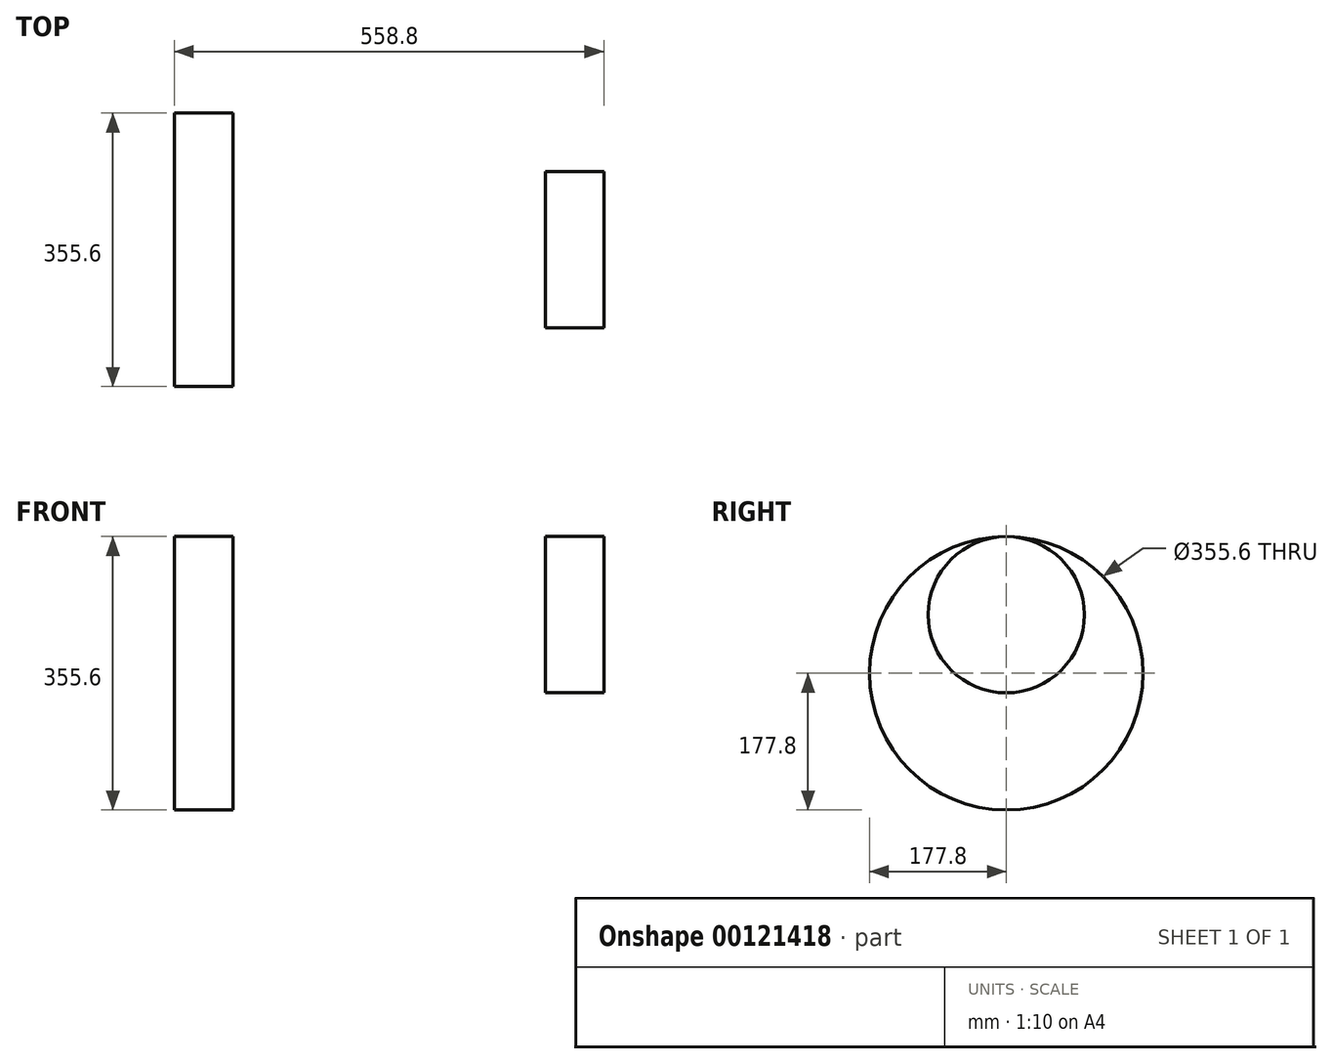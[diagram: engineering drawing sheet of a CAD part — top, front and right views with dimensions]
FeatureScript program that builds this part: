
annotation { "Feature Type Name" : "Feature", "Feature Type Description" : "" }
export const myFeature = defineFeature(function(context is Context, id is Id, definition is map)
    precondition{}
    {
        {
            var Q0;
            Q0=qCreatedBy(makeId("Right.planeOp"),FACE);
            cPlane(context, id + "F0", {"entities" : qUnion([Q0]), "cplaneType" : CPlaneType.OFFSET, "offset" : 406.4 * mm, "width" : 152.4 * mm, "height" : 152.4 * mm});
        }
        {
            var Q0;
            Q0=qCreatedBy(makeId("Front.planeOp"),FACE);
            var sketch = newSketch(context, id + "F1", { "sketchPlane" : qUnion([Q0])});
            skLineSegment(sketch, "E0.bottom", {"start": v(0, 203.2) * mm, "end": v(406.4, 203.2) * mm});
            skLineSegment(sketch, "E0.top", {"start": v(0, 0) * mm, "end": v(406.4, 0) * mm});
            skLineSegment(sketch, "E0.left", {"start": v(0, 203.2) * mm, "end": v(0, 0) * mm});
            skLineSegment(sketch, "E0.right", {"start": v(406.4, 203.2) * mm, "end": v(406.4, 0) * mm});
            skLineSegment(sketch, "E1.left", {"start": v(0, 0) * mm, "end": v(0, -152.4) * mm});
            skLineSegment(sketch, "E1.right", {"start": v(406.4, 0) * mm, "end": v(406.4, -152.4) * mm});
            skPoint(sketch, "E2", {"position": v(0, 0) * mm});
            skFitSpline(sketch, "E3", {"points": [v(0, -152.4) * mm, v(406.4, 0) * mm], "startDerivative": vector(696.83, 0) * mm, "endDerivative": vector(541.42, 0) * mm});
            skSolve(sketch);
        }
        {
            var Q0;
            Q0=qCreatedBy(makeId("Right.planeOp"),FACE);
            var sketch = newSketch(context, id + "F2", { "sketchPlane" : qUnion([Q0])});
            skCircle(sketch, "E4", {"center": v(0, 25.4) * mm, "radius": 177.8 * mm});
            skSolve(sketch);
        }
        {
            var Q0;
            Q0=qCreatedBy(id+"F0.planeOp",FACE);
            var sketch = newSketch(context, id + "F3", { "sketchPlane" : qUnion([Q0])});
            skCircle(sketch, "E5", {"center": v(0, 101.6) * mm, "radius": 101.6 * mm});
            skSolve(sketch);
        }
        {
            var Q0;
            Q0=sQuery(id+"F2.wireOp",EDGE,"E4");
            extrude(context, id + "F4", {"bodyType" : ToolBodyType.SURFACE, "surfaceEntities" : qUnion([Q0]), "oppositeDirection" : true, "depth" : 76.2 * mm});
        }
        {
            var Q0;
            Q0=sQuery(id+"F3.wireOp",EDGE,"E5");
            extrude(context, id + "F5", {"bodyType" : ToolBodyType.SURFACE, "surfaceEntities" : qUnion([Q0]), "depth" : 76.2 * mm});
        }
    });
